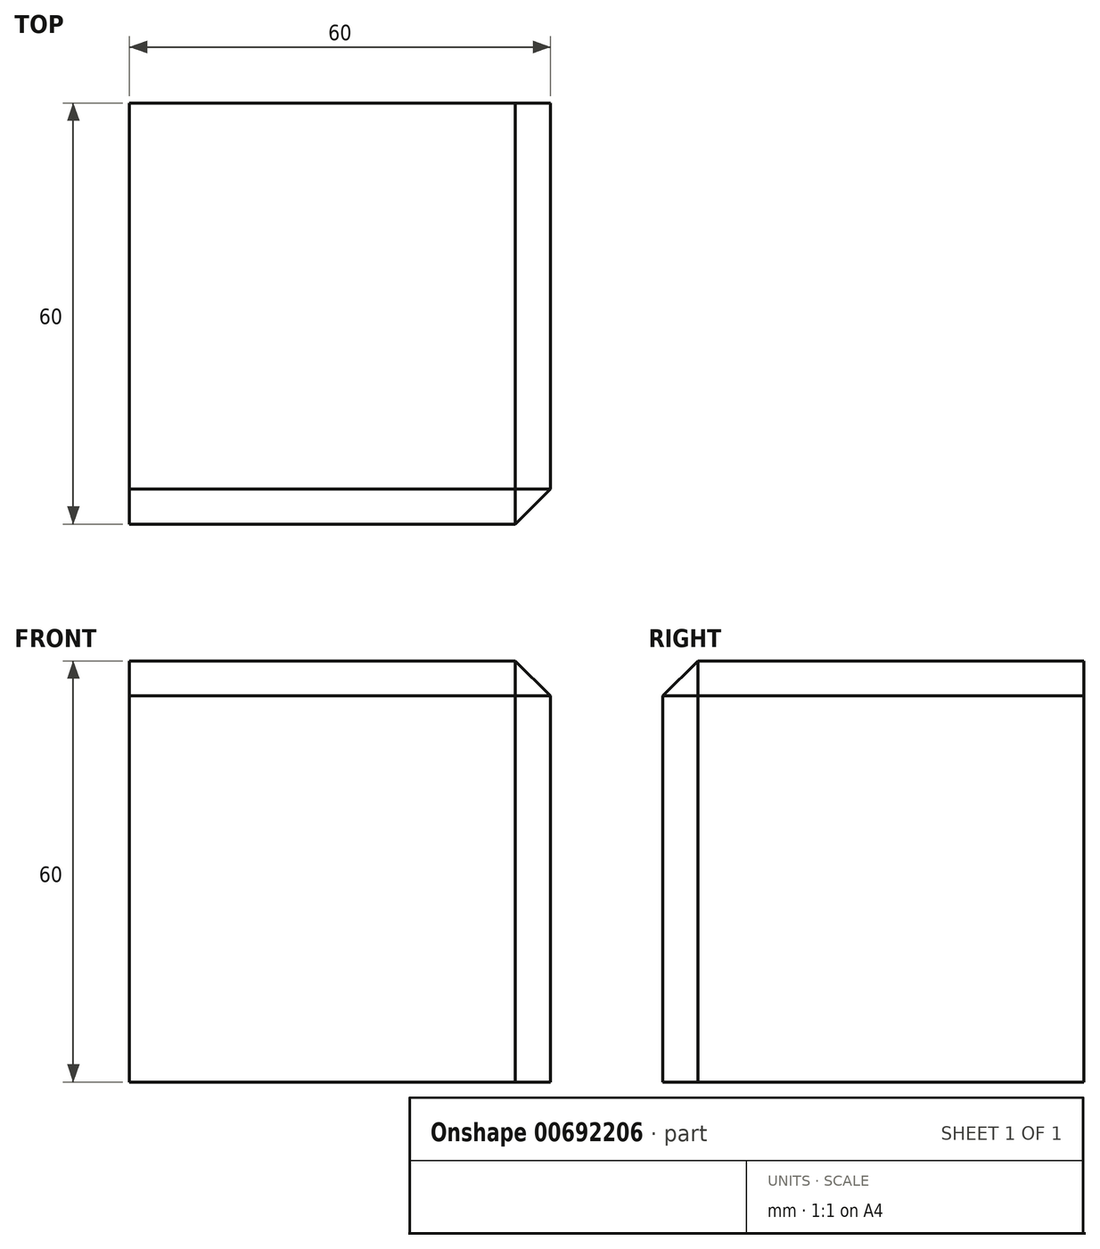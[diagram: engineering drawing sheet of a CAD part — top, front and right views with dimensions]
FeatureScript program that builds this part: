
annotation { "Feature Type Name" : "Feature", "Feature Type Description" : "" }
export const myFeature = defineFeature(function(context is Context, id is Id, definition is map)
    precondition{}
    {
        {
            var Q0;
            Q0=qCreatedBy(makeId("Front.planeOp"),FACE);
            var sketch = newSketch(context, id + "F0", { "sketchPlane" : qUnion([Q0])});
            skLineSegment(sketch, "E0.bottom", {"start": v(0, 0) * mm, "end": v(60, 0) * mm});
            skLineSegment(sketch, "E0.top", {"start": v(0, -60) * mm, "end": v(60, -60) * mm});
            skLineSegment(sketch, "E0.left", {"start": v(0, 0) * mm, "end": v(0, -60) * mm});
            skLineSegment(sketch, "E0.right", {"start": v(60, 0) * mm, "end": v(60, -60) * mm});
            skSolve(sketch);
        }
        {
            var Q0;
            Q0 = qSketchRegion(id + "F0", true);
            extrude(context, id + "F1", {"entities" : qUnion([Q0]), "depth" : 60 * mm, "offsetDistance" : 25 * mm});
        }
        {
            var Q0;
            Q0=makeQuery(id+"F1.opExtrude","CAP_EDGE",EDGE,{"disambiguationData":[OSD([sQuery(id+"F0.wireOp",EDGE,"E0.right")])],"isStart":false});
            var Q1;
            Q1=makeQuery(id+"F1.opExtrude","CAP_EDGE",EDGE,{"disambiguationData":[OSD([sQuery(id+"F0.wireOp",EDGE,"E0.bottom")])],"isStart":false});
            var Q2;
            Q2=makeQuery(id+"F1.opExtrude","SWEPT_EDGE",EDGE,{"disambiguationData":[OSD([sQuery(id+"F0.wireOp",EDGE,"E0.bottom"),sQuery(id+"F0.wireOp",EDGE,"E0.right")])]});
            chamfer(context, id + "F2", {"entities" : qUnion([Q0, Q1, Q2]), "width" : 5 * mm, "tangentPropagation" : true});
        }
    });
